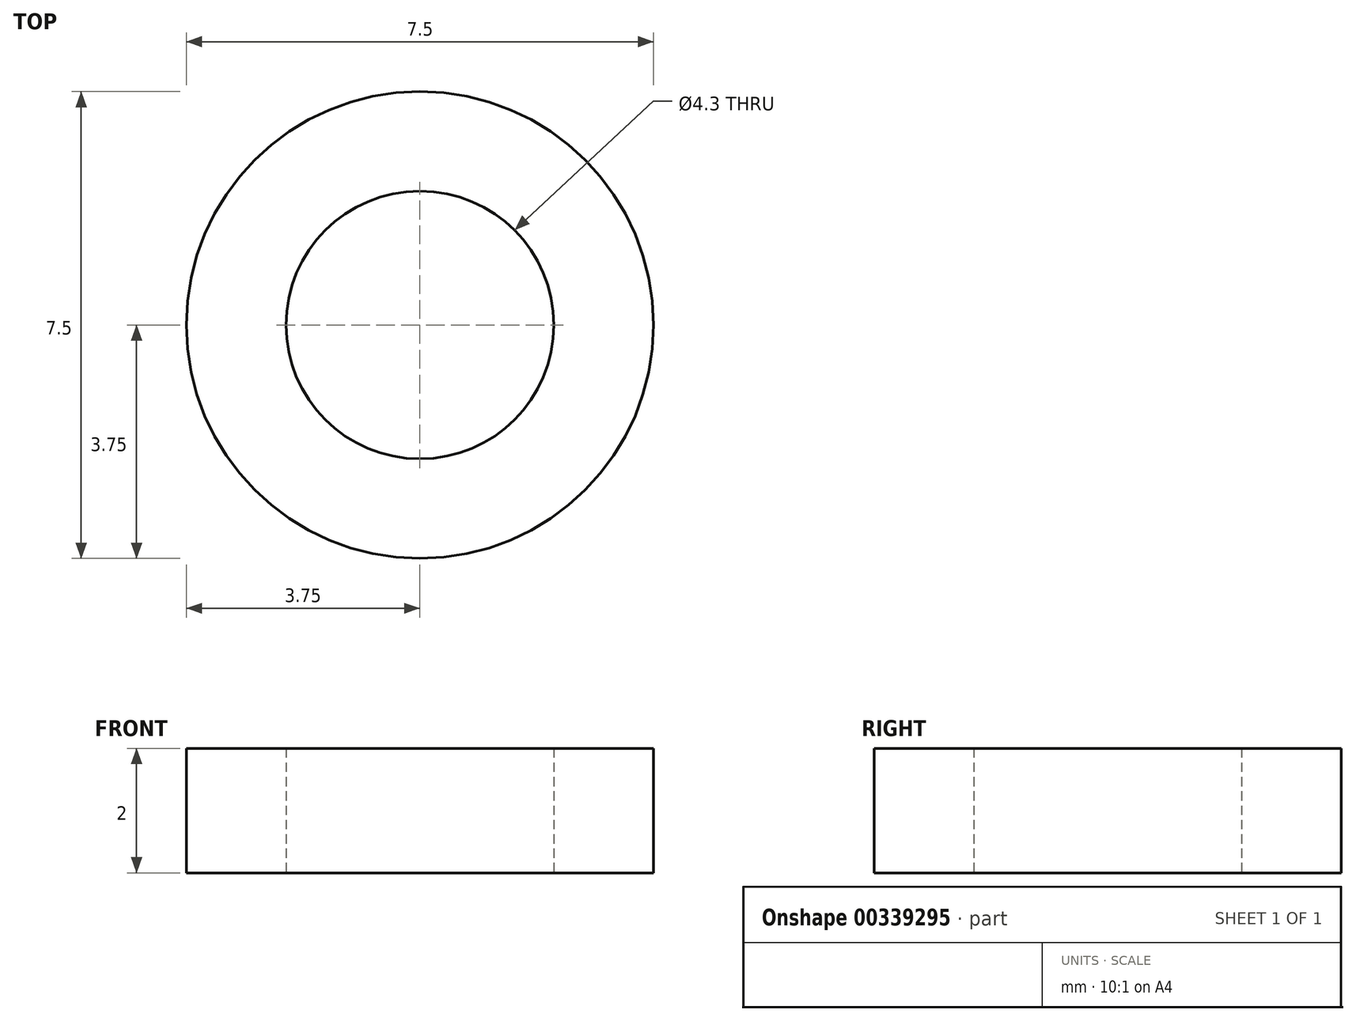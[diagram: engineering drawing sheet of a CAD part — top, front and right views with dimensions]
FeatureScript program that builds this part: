
annotation { "Feature Type Name" : "Feature", "Feature Type Description" : "" }
export const myFeature = defineFeature(function(context is Context, id is Id, definition is map)
    precondition{}
    {
        {
            var Q0;
            Q0=qCreatedBy(makeId("Top.planeOp"), FACE);
            var sketch = newSketch(context, id + "F0", { "sketchPlane" : qUnion([Q0])});
            skCircle(sketch, "E0", {"center": v(0, 0) * mm, "radius": 2.15 * mm});
            skCircle(sketch, "E1", {"center": v(0, 0) * mm, "radius": 3.75 * mm});
            skSolve(sketch);
        }
        {
            var Q0;
            Q0 = qSketchRegion(id + "F0", true);
            extrude(context, id + "F1", {"entities" : qUnion([Q0]), "depth" : 2 * mm, "offsetDistance" : 25 * mm});
        }
    });
